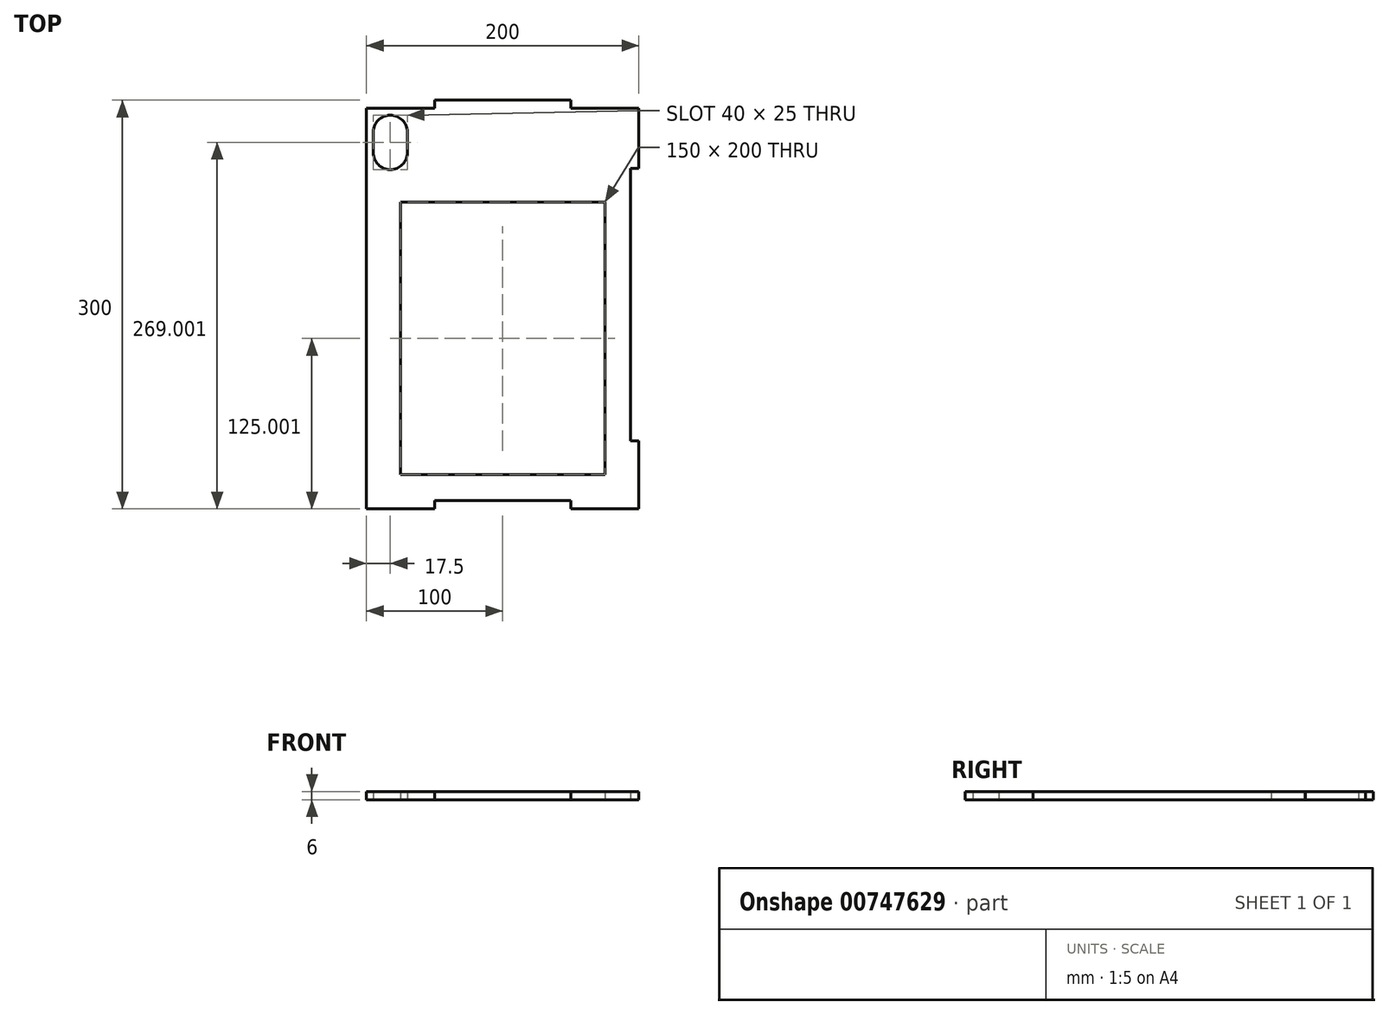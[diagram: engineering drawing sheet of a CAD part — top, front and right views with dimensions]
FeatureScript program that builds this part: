
annotation { "Feature Type Name" : "Feature", "Feature Type Description" : "" }
export const myFeature = defineFeature(function(context is Context, id is Id, definition is map)
    precondition{}
    {
        {
            var Q0;
            Q0=qCreatedBy(makeId("Top.planeOp"),FACE);
            var sketch = newSketch(context, id + "F0", { "sketchPlane" : qUnion([Q0])});
            skLineSegment(sketch, "E0.bottom", {"start": v(-50, 213.61) * mm, "end": v(0, 213.61) * mm});
            skLineSegment(sketch, "E0.top", {"start": v(-50, -80.39) * mm, "end": v(150, -80.39) * mm});
            skLineSegment(sketch, "E0.left", {"start": v(-50, 213.61) * mm, "end": v(-50, -80.39) * mm});
            skLineSegment(sketch, "E0.right", {"start": v(150, 213.61) * mm, "end": v(150, -80.39) * mm});
            skLineSegment(sketch, "E1.top", {"start": v(0, 219.61) * mm, "end": v(100, 219.61) * mm});
            skLineSegment(sketch, "E1.left", {"start": v(0, 213.61) * mm, "end": v(0, 219.61) * mm});
            skLineSegment(sketch, "E1.right", {"start": v(100, 213.61) * mm, "end": v(100, 219.61) * mm});
            skLineSegment(sketch, "E2.trimOffspring", {"start": v(100, 213.61) * mm, "end": v(150, 213.61) * mm});
            skLineSegment(sketch, "E3.bottom", {"start": v(150, 169.61) * mm, "end": v(144, 169.61) * mm});
            skLineSegment(sketch, "E3.top", {"start": v(150, -30.39) * mm, "end": v(144, -30.39) * mm});
            skLineSegment(sketch, "E3.left", {"start": v(150, 169.61) * mm, "end": v(150, -30.39) * mm});
            skLineSegment(sketch, "E3.right", {"start": v(144, 169.61) * mm, "end": v(144, -30.39) * mm});
            skLineSegment(sketch, "E4.bottom", {"start": v(-45, 196.11) * mm, "end": v(-20, 196.11) * mm});
            skLineSegment(sketch, "E4.top", {"start": v(-45, 181.11) * mm, "end": v(-20, 181.11) * mm});
            skLineSegment(sketch, "E4.left", {"start": v(-45, 196.11) * mm, "end": v(-45, 181.11) * mm});
            skLineSegment(sketch, "E4.right", {"start": v(-20, 196.11) * mm, "end": v(-20, 181.11) * mm});
            skArc(sketch, "E5", {"start": v(-20, 196.11) * mm, "mid": v(-32.5, 208.61) * mm, "end": v(-45, 196.11) * mm});
            skArc(sketch, "E6", {"start": v(-45, 181.11) * mm, "mid": v(-32.5, 168.61) * mm, "end": v(-20, 181.11) * mm});
            skLineSegment(sketch, "E7.bottom", {"start": v(-25, 144.61) * mm, "end": v(125, 144.61) * mm});
            skLineSegment(sketch, "E7.top", {"start": v(-25, -55.39) * mm, "end": v(125, -55.39) * mm});
            skLineSegment(sketch, "E7.left", {"start": v(-25, 144.61) * mm, "end": v(-25, -55.39) * mm});
            skLineSegment(sketch, "E7.right", {"start": v(125, 144.61) * mm, "end": v(125, -55.39) * mm});
            skLineSegment(sketch, "E8", {"start": v(79.74, -55.39) * mm, "end": v(79.74, -80.39) * mm, "construction": true});
            skLineSegment(sketch, "E9", {"start": v(125, 43.58) * mm, "end": v(150, 43.58) * mm, "construction": true});
            skLineSegment(sketch, "E10", {"start": v(-50, 44.37) * mm, "end": v(-25, 44.37) * mm, "construction": true});
            skLineSegment(sketch, "E11", {"start": v(0, -80.39) * mm, "end": v(0, -74.39) * mm});
            skLineSegment(sketch, "E12", {"start": v(0, -74.39) * mm, "end": v(100, -74.39) * mm});
            skLineSegment(sketch, "E13", {"start": v(100, -74.39) * mm, "end": v(100, -80.39) * mm});
            skSolve(sketch);
        }
        {
            var Q0;
            Q0=makeQuery(id+"F0.imprint","IMPRINT",FACE,{"disambiguationData":[TD([[makeQuery(id+"F0.imprint","IMPRINT",EDGE,{"derivedFrom":sQuery(id+"F0.wireOp",EDGE,"E0.bottom")}),-1.0]])]});
            extrude(context, id + "F1", {"entities" : qUnion([Q0]), "depth" : 6 * mm, "offsetDistance" : 25.4 * mm});
        }
    });
